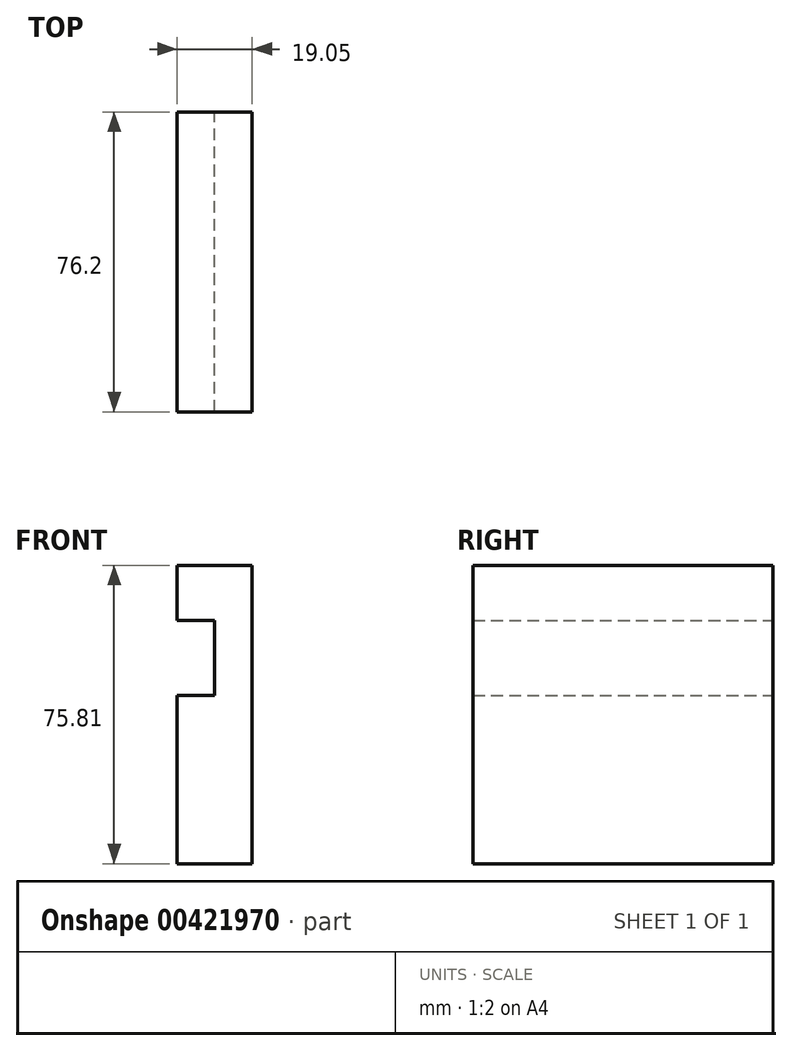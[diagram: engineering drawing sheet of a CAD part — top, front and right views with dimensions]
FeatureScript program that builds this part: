
annotation { "Feature Type Name" : "Feature", "Feature Type Description" : "" }
export const myFeature = defineFeature(function(context is Context, id is Id, definition is map)
    precondition{}
    {
        {
            var Q0;
            Q0=qCreatedBy(makeId("Front.planeOp"),FACE);
            var sketch = newSketch(context, id + "F0", { "sketchPlane" : qUnion([Q0])});
            skLineSegment(sketch, "E0", {"start": v(0, 0) * mm, "end": v(-19.05, 0) * mm});
            skLineSegment(sketch, "E1", {"start": v(-19.05, 0) * mm, "end": v(-19.05, 42.77) * mm});
            skLineSegment(sketch, "E2", {"start": v(-19.05, 42.77) * mm, "end": v(-9.53, 42.77) * mm});
            skLineSegment(sketch, "E3", {"start": v(-9.53, 42.77) * mm, "end": v(-9.53, 61.82) * mm});
            skLineSegment(sketch, "E4", {"start": v(-9.53, 61.82) * mm, "end": v(-19.05, 61.82) * mm});
            skLineSegment(sketch, "E5", {"start": v(-19.05, 61.82) * mm, "end": v(-19.05, 75.8) * mm});
            skLineSegment(sketch, "E6", {"start": v(-19.05, 75.8) * mm, "end": v(0, 75.8) * mm});
            skLineSegment(sketch, "E7", {"start": v(0, 75.8) * mm, "end": v(0, 0) * mm});
            skSolve(sketch);
        }
        {
            var Q0;
            Q0=makeQuery(id+"F0.imprint","IMPRINT",FACE,{"disambiguationData":[TD([[makeQuery(id+"F0.imprint","IMPRINT",EDGE,{"derivedFrom":sQuery(id+"F0.wireOp",EDGE,"E0")}),-1.0]])]});
            extrude(context, id + "F1", {"entities" : qUnion([Q0]), "depth" : 76.2 * mm});
        }
    });
